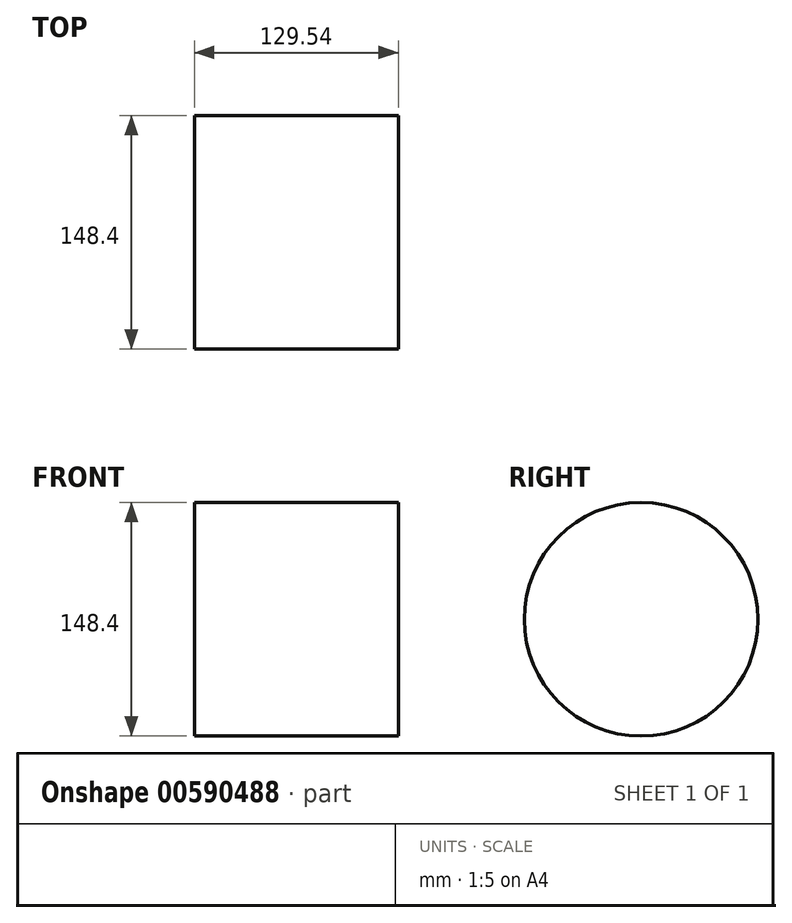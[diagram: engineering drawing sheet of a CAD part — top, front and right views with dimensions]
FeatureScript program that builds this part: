
annotation { "Feature Type Name" : "Feature", "Feature Type Description" : "" }
export const myFeature = defineFeature(function(context is Context, id is Id, definition is map)
    precondition{}
    {
        {
            var Q0;
            Q0=qCreatedBy(makeId("Right.planeOp"),FACE);
            var sketch = newSketch(context, id + "F0", { "sketchPlane" : qUnion([Q0])});
            skCircle(sketch, "E0", {"center": v(51.57, -53.35) * mm, "radius": 74.2 * mm});
            skPoint(sketch, "E0.first.point", {"position": v(0, 0) * mm});
            skPoint(sketch, "E0.second.point", {"position": v(118.74, -84.87) * mm});
            skPoint(sketch, "E0.third.point", {"position": v(26.72, -123.26) * mm});
            skSolve(sketch);
        }
        {
            var Q0;
            Q0 = qSketchRegion(id + "F0", true);
            extrude(context, id + "F1", {"entities" : qUnion([Q0]), "depth" : 25.4 * mm, "offsetDistance" : 25.4 * mm});
        }
        {
            var Q0;
            Q0=makeQuery(id+"F1.opExtrude","CAP_FACE",FACE,{"disambiguationData":[OSD([sQuery(id+"F0.wireOp",EDGE,"E0")])],"isStart":false});
            extrude(context, id + "F2", {"entities" : qUnion([Q0]), "operationType" : NewBodyOperationType.ADD, "depth" : 104.14 * mm, "offsetDistance" : 25.4 * mm});
        }
    });
